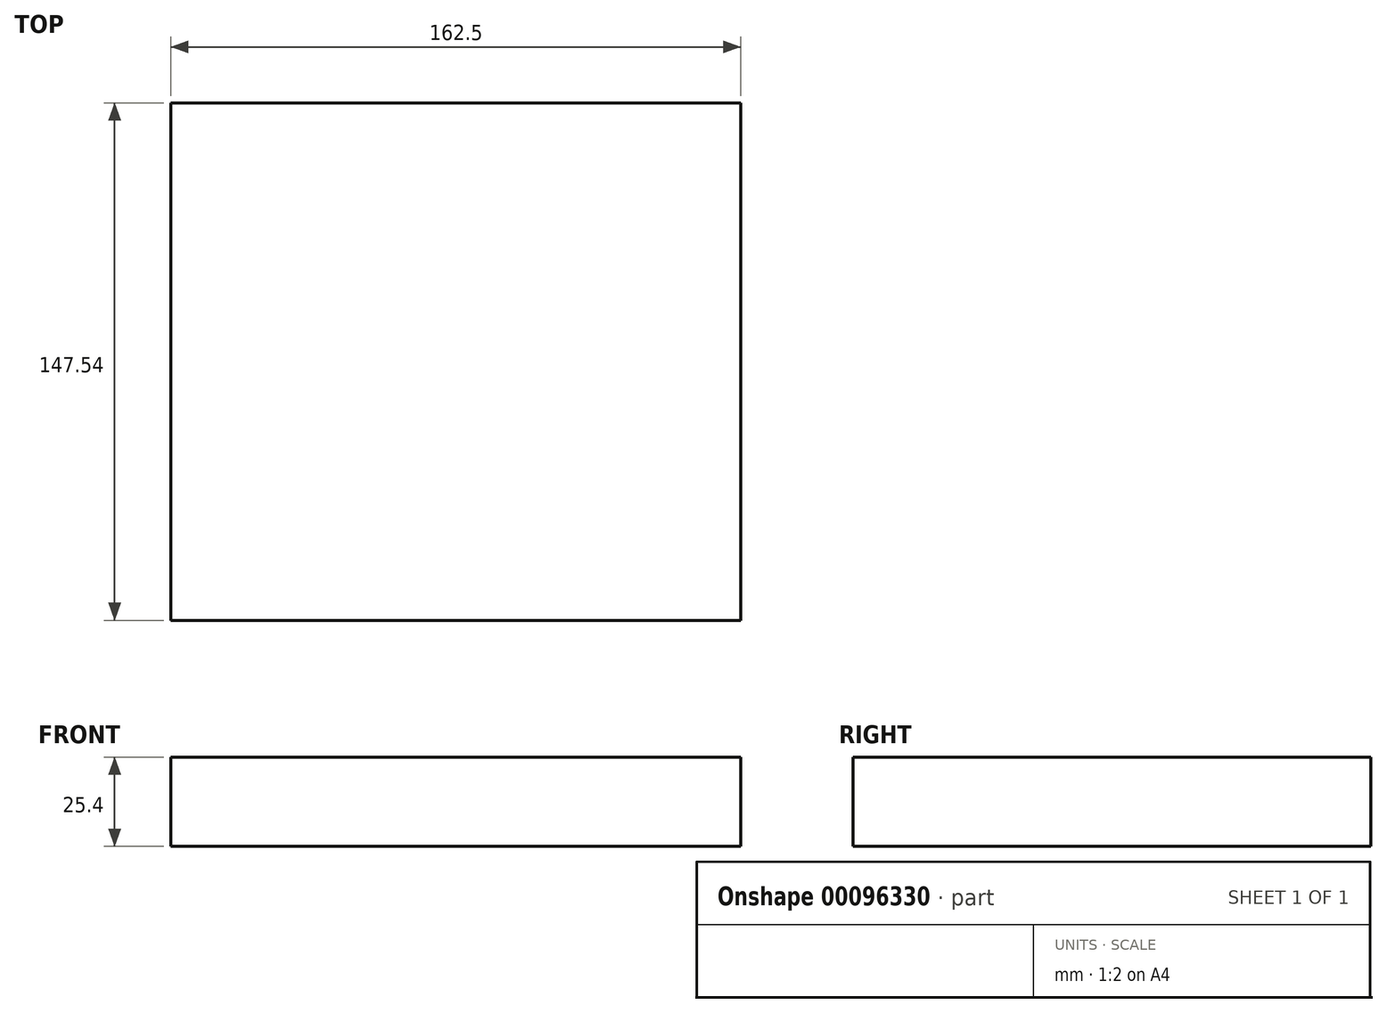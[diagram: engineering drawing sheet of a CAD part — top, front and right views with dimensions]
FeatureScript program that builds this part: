
annotation { "Feature Type Name" : "Feature", "Feature Type Description" : "" }
export const myFeature = defineFeature(function(context is Context, id is Id, definition is map)
    precondition{}
    {
        {
            var Q0;
            Q0=qCreatedBy(makeId("Top.planeOp"),FACE);
            var sketch = newSketch(context, id + "F0", { "sketchPlane" : qUnion([Q0])});
            skLineSegment(sketch, "E0.bottom", {"start": v(81.25, -73.77) * mm, "end": v(-81.25, -73.77) * mm});
            skLineSegment(sketch, "E0.top", {"start": v(81.25, 73.77) * mm, "end": v(-81.25, 73.77) * mm});
            skLineSegment(sketch, "E0.left", {"start": v(81.25, -73.77) * mm, "end": v(81.25, 73.77) * mm});
            skLineSegment(sketch, "E0.right", {"start": v(-81.25, -73.77) * mm, "end": v(-81.25, 73.77) * mm});
            skPoint(sketch, "E0.middle", {"position": v(0, 0) * mm});
            skSolve(sketch);
        }
        {
            var Q0;
            Q0=makeQuery(id+"F0.imprint","IMPRINT",FACE,{"disambiguationData":[TD([[makeQuery(id+"F0.imprint","IMPRINT",EDGE,{"derivedFrom":sQuery(id+"F0.wireOp",EDGE,"E0.bottom")}),-1.0]])]});
            extrude(context, id + "F1", {"entities" : qUnion([Q0]), "depth" : 25.4 * mm});
        }
        {
            var Q0;
            Q0=makeQuery(id+"F1.opExtrude","CAP_FACE",FACE,{"disambiguationData":[OSD([sQuery(id+"F0.wireOp",EDGE,"E0.bottom"),sQuery(id+"F0.wireOp",EDGE,"E0.top"),sQuery(id+"F0.wireOp",EDGE,"E0.left"),sQuery(id+"F0.wireOp",EDGE,"E0.right")])],"isStart":true});
            var sketch = newSketch(context, id + "F2", { "sketchPlane" : qUnion([Q0])});
            skCircle(sketch, "E1", {"center": v(0, 0) * mm, "radius": 30.64 * mm});
            skSolve(sketch);
        }
        {
            var Q0;
            Q0=makeQuery(id+"F2.imprint","IMPRINT",FACE,{"disambiguationData":[TD([[makeQuery(id+"F2.imprint","IMPRINT",EDGE,{"derivedFrom":sQuery(id+"F2.wireOp",EDGE,"E1")}),1.0]])]});
            extrude(context, id + "F3", {"entities" : qUnion([Q0]), "operationType" : NewBodyOperationType.ADD, "oppositeDirection" : true, "depth" : 4 * mm});
        }
    });
